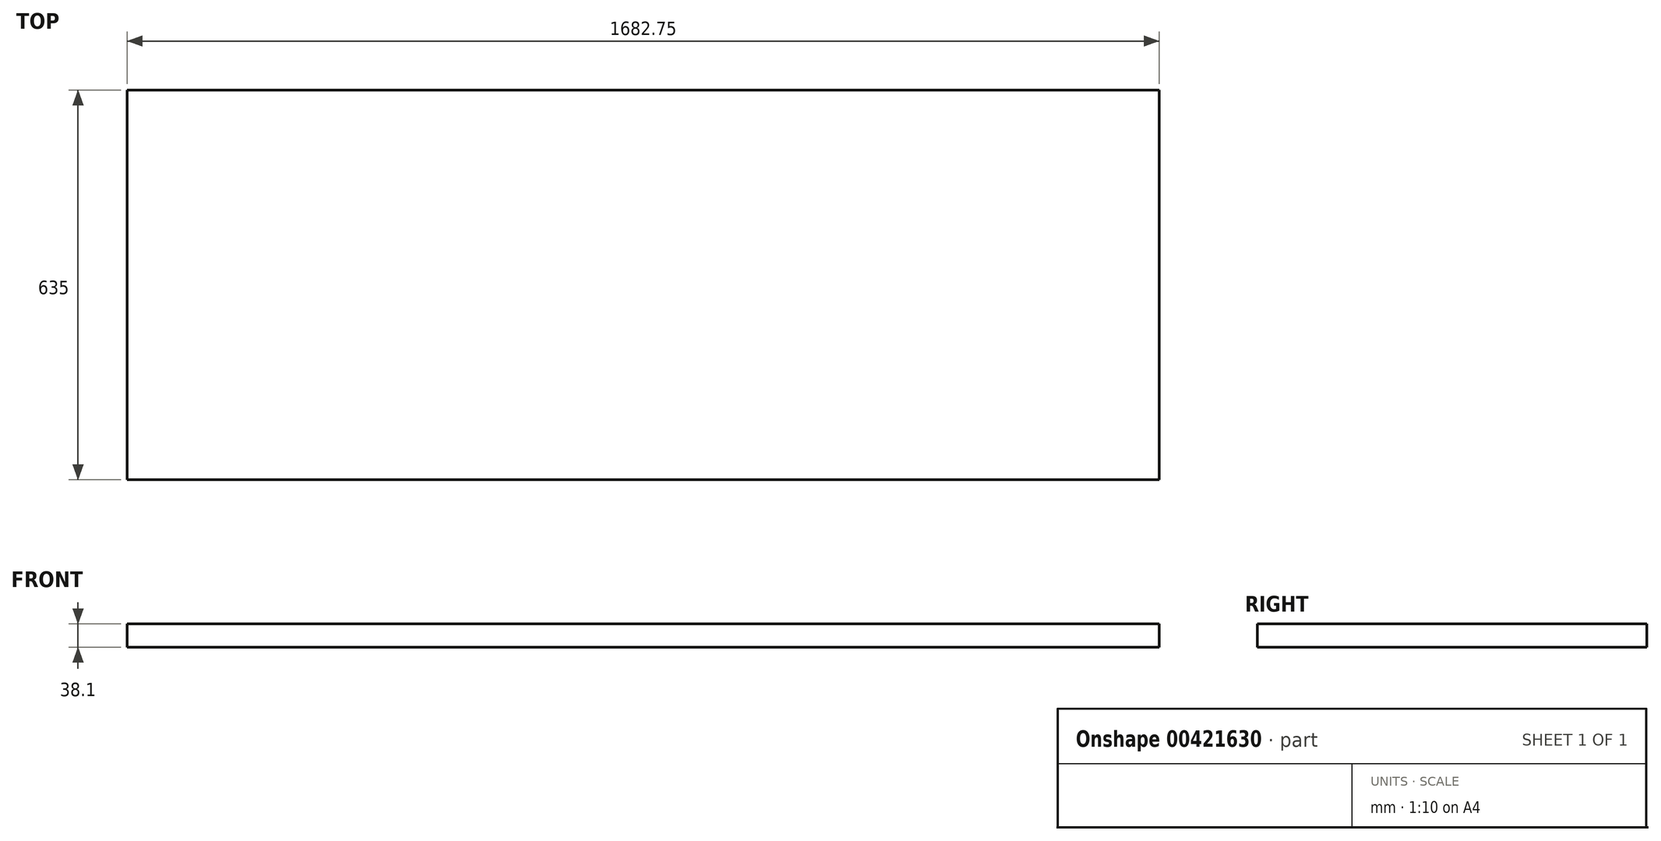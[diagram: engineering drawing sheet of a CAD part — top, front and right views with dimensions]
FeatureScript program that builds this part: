
annotation { "Feature Type Name" : "Feature", "Feature Type Description" : "" }
export const myFeature = defineFeature(function(context is Context, id is Id, definition is map)
    precondition{}
    {
        {
            var Q0;
            Q0=qCreatedBy(makeId("Front.planeOp"),FACE);
            var sketch = newSketch(context, id + "F0", { "sketchPlane" : qUnion([Q0])});
            skLineSegment(sketch, "E0.bottom", {"start": v(0, 0) * mm, "end": v(1682.75, 0) * mm});
            skLineSegment(sketch, "E0.top", {"start": v(0, 38.1) * mm, "end": v(1682.75, 38.1) * mm});
            skLineSegment(sketch, "E0.left", {"start": v(0, 0) * mm, "end": v(0, 38.1) * mm});
            skLineSegment(sketch, "E0.right", {"start": v(1682.75, 0) * mm, "end": v(1682.75, 38.1) * mm});
            skSolve(sketch);
        }
        {
            var Q0;
            Q0 = qSketchRegion(id + "F0", true);
            extrude(context, id + "F1", {"entities" : qUnion([Q0]), "depth" : 635 * mm});
        }
    });
